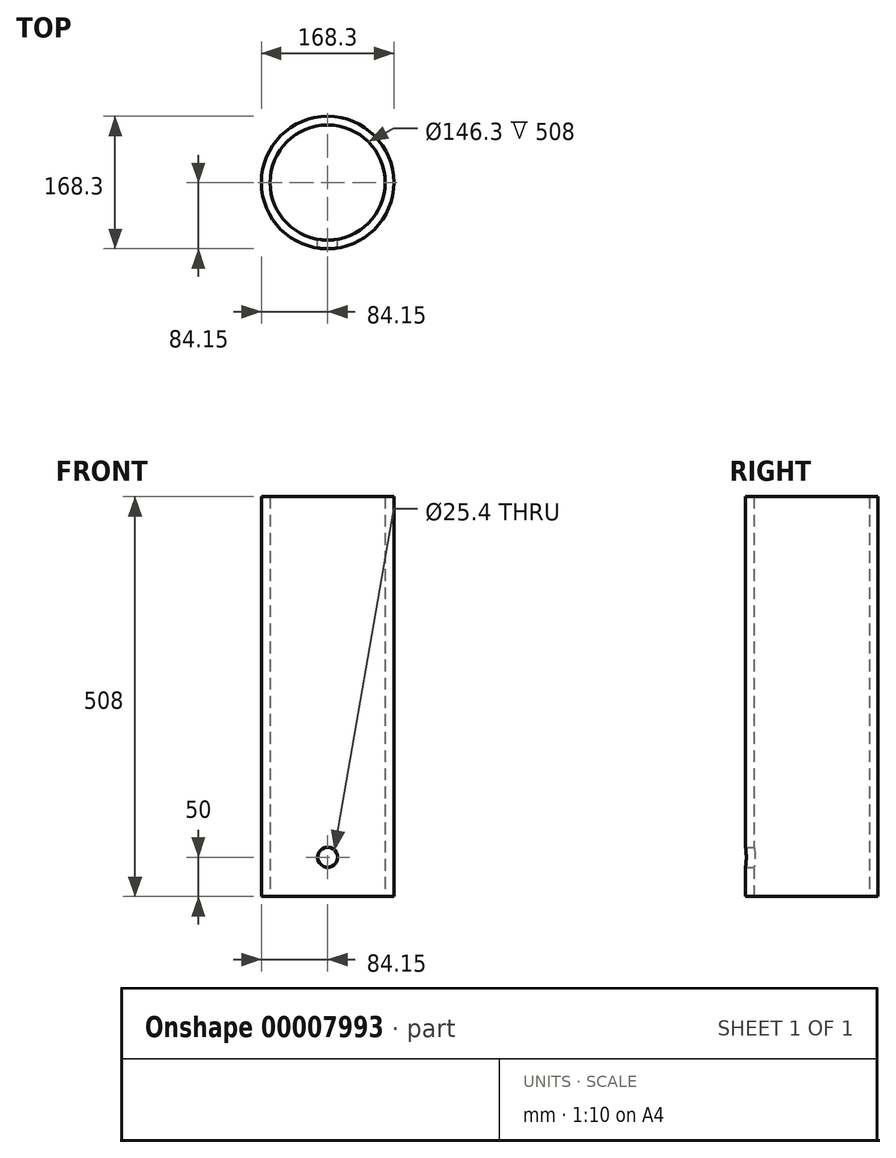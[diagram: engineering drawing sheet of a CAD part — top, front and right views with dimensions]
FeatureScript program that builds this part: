
annotation { "Feature Type Name" : "Feature", "Feature Type Description" : "" }
export const myFeature = defineFeature(function(context is Context, id is Id, definition is map)
    precondition{}
    {
        {
            var Q0;
            Q0=qCreatedBy(makeId("Top.planeOp"),FACE);
            var sketch = newSketch(context, id + "F0", { "sketchPlane" : qUnion([Q0])});
            skCircle(sketch, "E0", {"center": v(0, 0) * mm, "radius": 84.15 * mm});
            skCircle(sketch, "E1", {"center": v(0, 0) * mm, "radius": 73.15 * mm});
            skCircle(sketch, "E2", {"center": v(0, 0) * mm, "radius": 139.7 * mm});
            skSolve(sketch);
        }
        {
            var Q0;
            Q0=makeQuery(id+"F0.imprint","IMPRINT",FACE,{"disambiguationData":[TD([[makeQuery(id+"F0.imprint","IMPRINT",EDGE,{"derivedFrom":sQuery(id+"F0.wireOp",EDGE,"E0")}),1.0]])]});
            extrude(context, id + "F1", {"entities" : qUnion([Q0]), "depth" : 508 * mm});
        }
        {
            var Q0;
            Q0=qCreatedBy(makeId("Front.planeOp"),FACE);
            var sketch = newSketch(context, id + "F2", { "sketchPlane" : qUnion([Q0])});
            skCircle(sketch, "E3", {"center": v(0, 50) * mm, "radius": 12.7 * mm});
            skSolve(sketch);
        }
        {
            var Q0;
            Q0=makeQuery(id+"F2.imprint","IMPRINT",FACE,{"disambiguationData":[TD([[makeQuery(id+"F2.imprint","IMPRINT",EDGE,{"derivedFrom":sQuery(id+"F2.wireOp",EDGE,"E3")}),1.0]])]});
            extrude(context, id + "F3", {"entities" : qUnion([Q0]), "operationType" : NewBodyOperationType.REMOVE, "endBound" : BoundingType.THROUGH_ALL, "depth" : 25 * mm});
        }
    });
